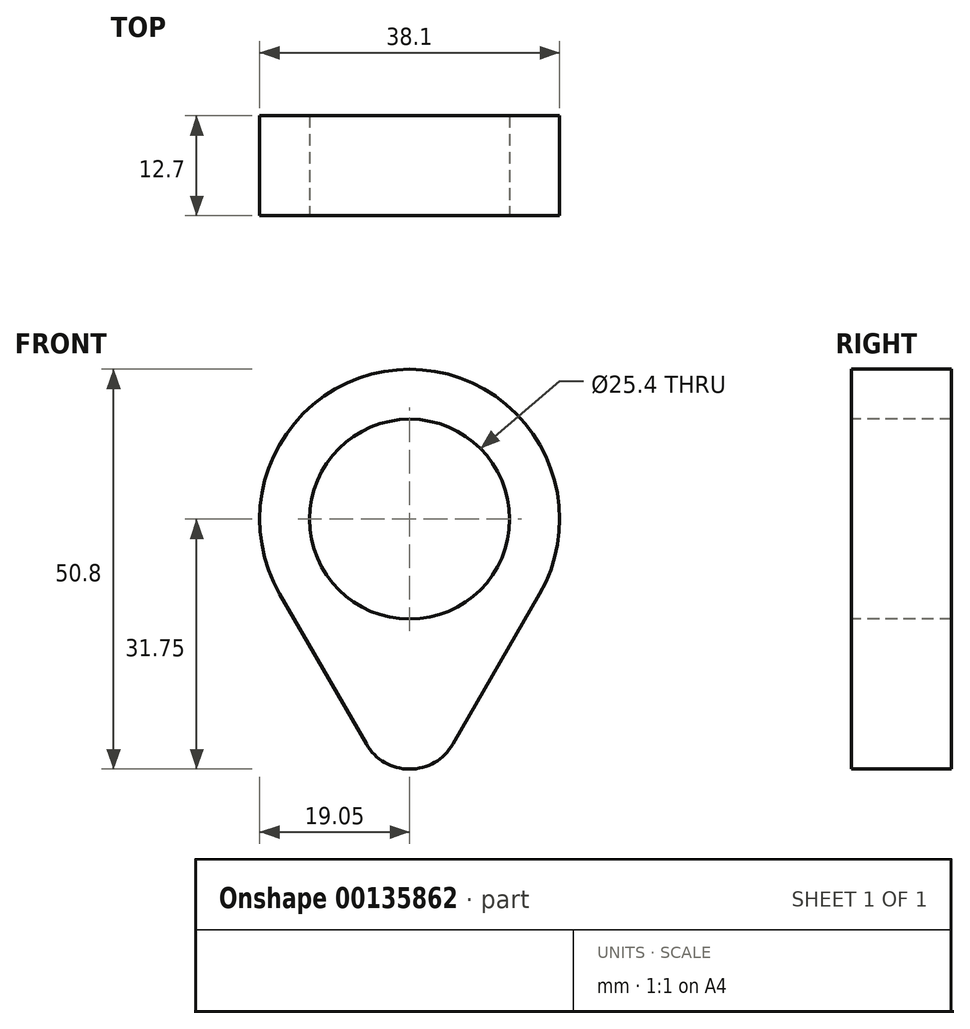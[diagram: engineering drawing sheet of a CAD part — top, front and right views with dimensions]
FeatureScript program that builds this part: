
annotation { "Feature Type Name" : "Feature", "Feature Type Description" : "" }
export const myFeature = defineFeature(function(context is Context, id is Id, definition is map)
    precondition{}
    {
        {
            var Q0;
            Q0=qCreatedBy(makeId("Front.planeOp"),FACE);
            cPlane(context, id + "F0", {"entities" : qUnion([Q0]), "cplaneType" : CPlaneType.OFFSET, "offset" : 63.5 * mm, "width" : 152.4 * mm, "height" : 152.4 * mm});
        }
        {
            var Q0;
            Q0=qCreatedBy(id+"F0.planeOp",FACE);
            var sketch = newSketch(context, id + "F1", { "sketchPlane" : qUnion([Q0])});
            skCircle(sketch, "E0", {"center": v(0, 0) * mm, "radius": 12.7 * mm});
            skArc(sketch, "E1", {"start": v(16.5, -9.53) * mm, "mid": v(0, 19.05) * mm, "end": v(-16.5, -9.52) * mm});
            skArc(sketch, "E2", {"start": v(-5.5, -28.58) * mm, "mid": v(0, -31.75) * mm, "end": v(5.5, -28.58) * mm});
            skLineSegment(sketch, "E3", {"start": v(-5.5, -28.58) * mm, "end": v(-16.5, -9.52) * mm});
            skLineSegment(sketch, "E4", {"start": v(5.5, -28.58) * mm, "end": v(16.5, -9.53) * mm});
            skSolve(sketch);
        }
        {
            var Q0;
            Q0=makeQuery(id+"F1.imprint","IMPRINT",FACE,{"disambiguationData":[TD([[makeQuery(id+"F1.imprint","IMPRINT",EDGE,{"derivedFrom":sQuery(id+"F1.wireOp",EDGE,"E0")}),-1.0]])]});
            extrude(context, id + "F2", {"entities" : qUnion([Q0]), "oppositeDirection" : true, "depth" : 12.7 * mm});
        }
    });
